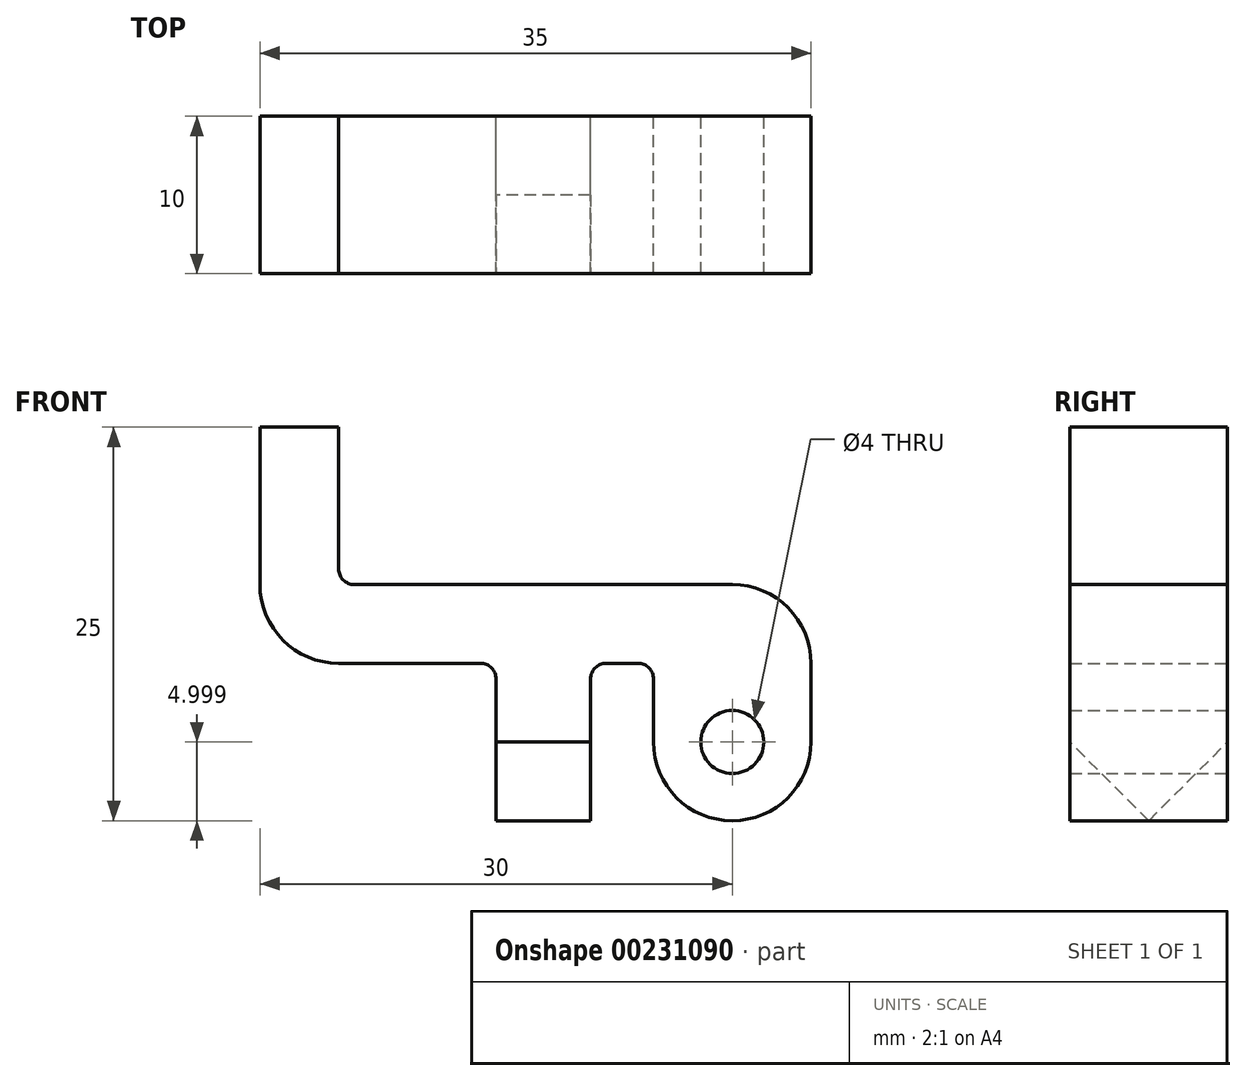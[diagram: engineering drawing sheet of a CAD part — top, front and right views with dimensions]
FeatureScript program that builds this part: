
annotation { "Feature Type Name" : "Feature", "Feature Type Description" : "" }
export const myFeature = defineFeature(function(context is Context, id is Id, definition is map)
    precondition{}
    {
        {
            var Q0;
            Q0=qCreatedBy(makeId("Front.planeOp"),FACE);
            var sketch = newSketch(context, id + "F0", { "sketchPlane" : qUnion([Q0])});
            skLineSegment(sketch, "E0", {"start": v(0, 18.54) * mm, "end": v(0, 8.54) * mm});
            skLineSegment(sketch, "E1", {"start": v(5, 3.54) * mm, "end": v(14, 3.54) * mm});
            skLineSegment(sketch, "E2", {"start": v(15, 2.54) * mm, "end": v(15, -6.46) * mm});
            skLineSegment(sketch, "E3", {"start": v(15, -6.46) * mm, "end": v(21, -6.46) * mm});
            skLineSegment(sketch, "E4", {"start": v(21, -6.46) * mm, "end": v(21, 2.54) * mm});
            skLineSegment(sketch, "E5", {"start": v(22, 3.54) * mm, "end": v(24, 3.54) * mm});
            skLineSegment(sketch, "E6", {"start": v(25, 2.54) * mm, "end": v(25, -1.46) * mm});
            skLineSegment(sketch, "E7", {"start": v(30, -6.46) * mm, "end": v(30, -6.46) * mm});
            skLineSegment(sketch, "E8", {"start": v(35, -1.46) * mm, "end": v(35, 3.54) * mm});
            skLineSegment(sketch, "E9", {"start": v(30, 8.54) * mm, "end": v(5, 8.54) * mm});
            skLineSegment(sketch, "E10", {"start": v(5, 8.54) * mm, "end": v(5, 18.54) * mm});
            skLineSegment(sketch, "E11", {"start": v(5, 18.54) * mm, "end": v(0, 18.54) * mm});
            skCircle(sketch, "E12", {"center": v(30, -1.46) * mm, "radius": 2 * mm});
            skPoint(sketch, "E12.centerSnap0", {"position": v(30, -6.46) * mm});
            skPoint(sketch, "E13.visualSharp", {"position": v(35, -6.46) * mm});
            skArc(sketch, "E13.filletArc", {"start": v(30, -6.46) * mm, "mid": v(33.54, -5) * mm, "end": v(35, -1.46) * mm});
            skPoint(sketch, "E14.visualSharp", {"position": v(25, -6.46) * mm});
            skArc(sketch, "E14.filletArc", {"start": v(25, -1.46) * mm, "mid": v(26.46, -5) * mm, "end": v(30, -6.46) * mm});
            skPoint(sketch, "E15.visualSharp", {"position": v(35, 8.54) * mm});
            skArc(sketch, "E15.filletArc", {"start": v(35, 3.54) * mm, "mid": v(33.54, 7.07) * mm, "end": v(30, 8.54) * mm});
            skPoint(sketch, "E16.visualSharp", {"position": v(0, 3.54) * mm});
            skArc(sketch, "E16.filletArc", {"start": v(0, 8.54) * mm, "mid": v(1.46, 5) * mm, "end": v(5, 3.54) * mm});
            skPoint(sketch, "E17.visualSharp", {"position": v(15, 3.54) * mm});
            skArc(sketch, "E17.filletArc", {"start": v(15, 2.54) * mm, "mid": v(14.7, 3.25) * mm, "end": v(14, 3.54) * mm});
            skPoint(sketch, "E18.visualSharp", {"position": v(21, 3.54) * mm});
            skArc(sketch, "E18.filletArc", {"start": v(22, 3.54) * mm, "mid": v(21.3, 3.25) * mm, "end": v(21, 2.54) * mm});
            skPoint(sketch, "E19.visualSharp", {"position": v(25, 3.54) * mm});
            skArc(sketch, "E19.filletArc", {"start": v(25, 2.54) * mm, "mid": v(24.7, 3.25) * mm, "end": v(24, 3.54) * mm});
            skSolve(sketch);
        }
        {
            var Q0;
            Q0=makeQuery(id+"F0.imprint","IMPRINT",FACE,{"disambiguationData":[TD([[makeQuery(id+"F0.imprint","IMPRINT",EDGE,{"derivedFrom":sQuery(id+"F0.wireOp",EDGE,"E0")}),1.0]])]});
            extrude(context, id + "F1", {"entities" : qUnion([Q0]), "depth" : 10 * mm});
        }
        {
            var Q0;
            Q0=makeQuery(id+"F1.opExtrude","SWEPT_EDGE",EDGE,{"disambiguationData":[OSD([sQuery(id+"F0.wireOp",EDGE,"E9"),sQuery(id+"F0.wireOp",EDGE,"E10")])]});
            fillet(context, id + "F2", {"entities" : qUnion([Q0]), "radius" : 1 * mm, "tangentPropagation" : true, "allowEdgeOverflow" : false});
        }
        {
            var Q0;
            Q0=makeQuery(id+"F1.opExtrude","SWEPT_FACE",FACE,{"disambiguationData":[OSD([sQuery(id+"F0.wireOp",EDGE,"E2")])]});
            var sketch = newSketch(context, id + "F3", { "sketchPlane" : qUnion([Q0])});
            skLineSegment(sketch, "E20", {"start": v(5, -6.46) * mm, "end": v(10, -1.46) * mm});
            skLineSegment(sketch, "E21", {"start": v(5, -6.46) * mm, "end": v(0, -1.46) * mm});
            skLineSegment(sketch, "E22", {"start": v(5, -6.46) * mm, "end": v(5, 2.54) * mm});
            skSolve(sketch);
        }
        {
            var Q0;
            {var subQ0=sQuery(id+"F3.wireOp",EDGE,"E21");Q0=makeQuery(id+"F3.imprint","IMPRINT",FACE,{"disambiguationData":[TD([[makeQuery(id+"F3.imprint","IMPRINT",EDGE,{"derivedFrom":subQ0}),1.0]])]});}
            var Q1;
            {var subQ0=sQuery(id+"F3.wireOp",EDGE,"E20");Q1=makeQuery(id+"F3.imprint","IMPRINT",FACE,{"disambiguationData":[TD([[makeQuery(id+"F3.imprint","IMPRINT",EDGE,{"derivedFrom":subQ0}),-1.0]])]});}
            extrude(context, id + "F4", {"entities" : qUnion([Q0, Q1]), "operationType" : NewBodyOperationType.REMOVE, "oppositeDirection" : true, "depth" : 6 * mm});
        }
    });
